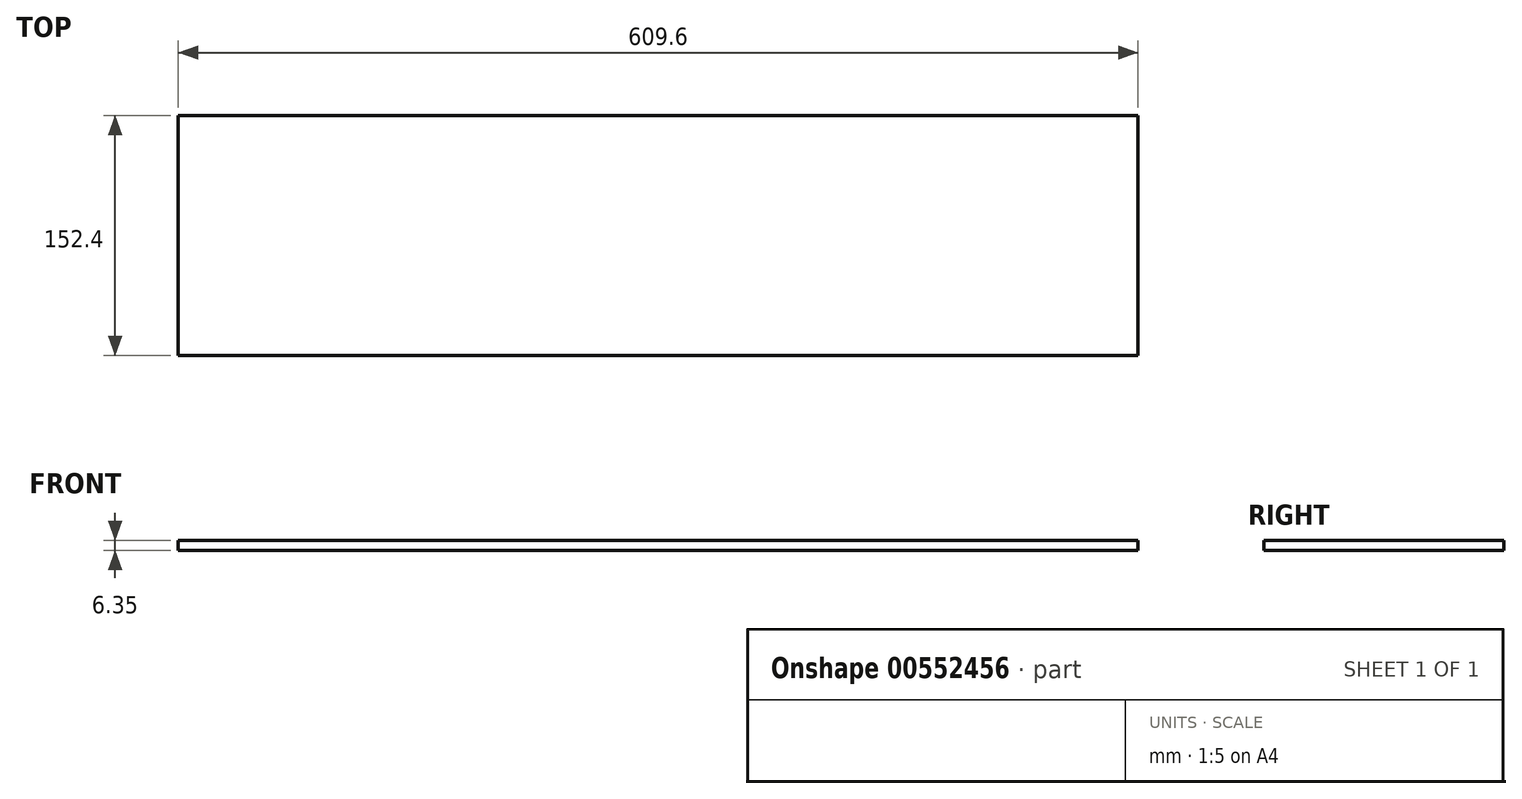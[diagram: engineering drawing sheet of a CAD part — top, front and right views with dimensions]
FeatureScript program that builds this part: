
annotation { "Feature Type Name" : "Feature", "Feature Type Description" : "" }
export const myFeature = defineFeature(function(context is Context, id is Id, definition is map)
    precondition{}
    {
        {
            var Q0;
            Q0=qCreatedBy(makeId("Front.planeOp"),FACE);
            var sketch = newSketch(context, id + "F0", { "sketchPlane" : qUnion([Q0])});
            skLineSegment(sketch, "E0.bottom", {"start": v(0, 0) * mm, "end": v(609.6, 0) * mm});
            skLineSegment(sketch, "E0.top", {"start": v(0, 6.35) * mm, "end": v(609.6, 6.35) * mm});
            skLineSegment(sketch, "E0.left", {"start": v(0, 0) * mm, "end": v(0, 6.35) * mm});
            skLineSegment(sketch, "E0.right", {"start": v(609.6, 0) * mm, "end": v(609.6, 6.35) * mm});
            skSolve(sketch);
        }
        {
            var Q0;
            Q0 = qSketchRegion(id + "F0", true);
            extrude(context, id + "F1", {"entities" : qUnion([Q0]), "depth" : 152.4 * mm, "offsetDistance" : 25.4 * mm});
        }
    });
